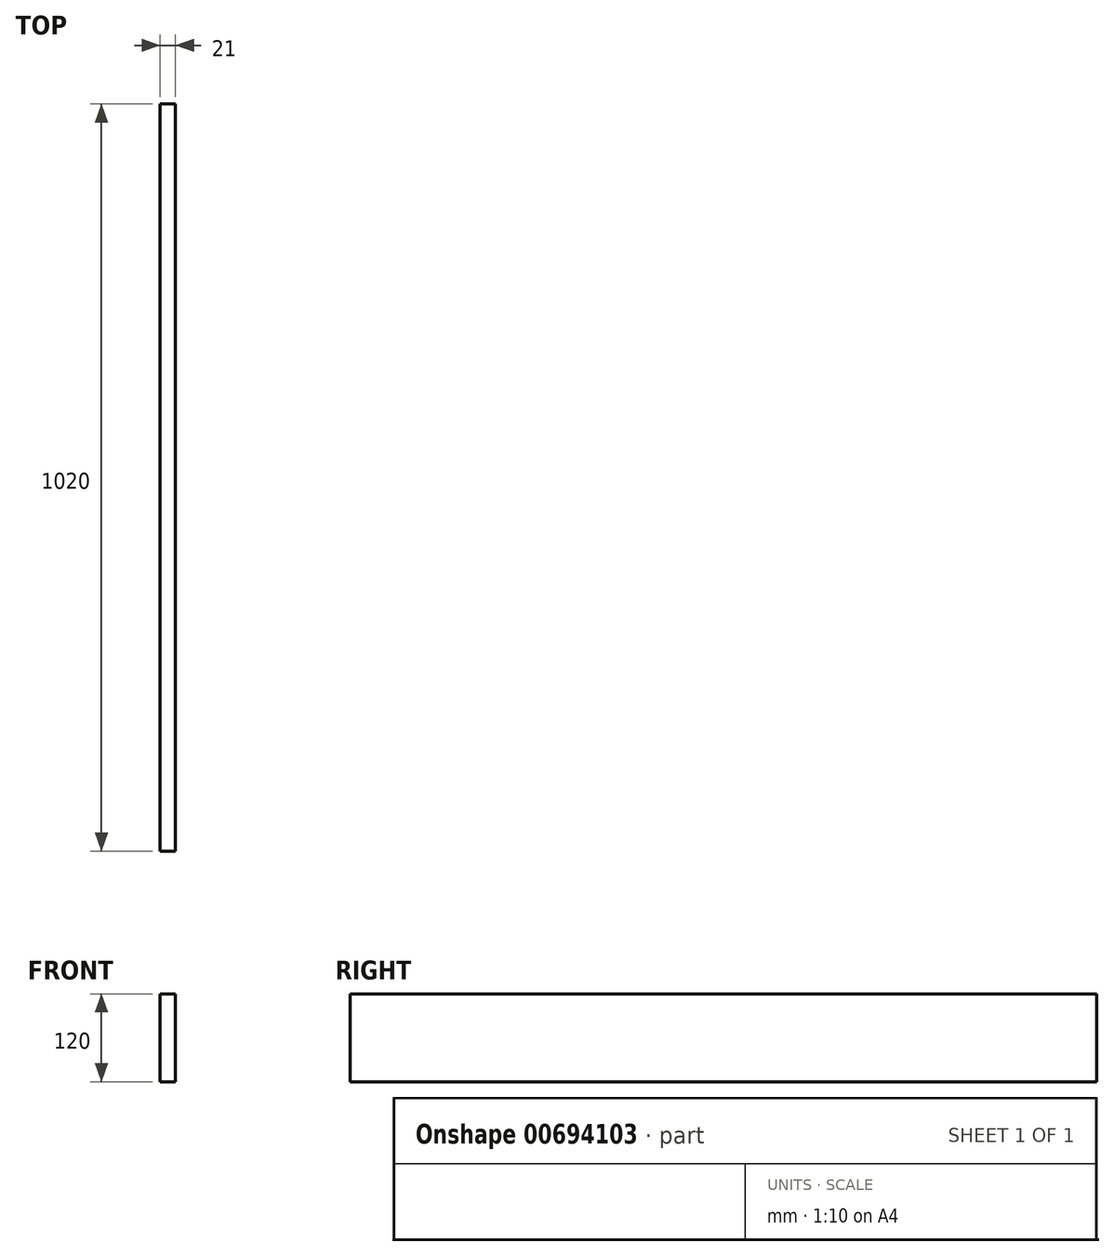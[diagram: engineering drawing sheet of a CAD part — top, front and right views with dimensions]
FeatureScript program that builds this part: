
annotation { "Feature Type Name" : "Feature", "Feature Type Description" : "" }
export const myFeature = defineFeature(function(context is Context, id is Id, definition is map)
    precondition{}
    {
        {
            var Q0;
            Q0=qCreatedBy(makeId("Right.planeOp"),FACE);
            var sketch = newSketch(context, id + "F0", { "sketchPlane" : qUnion([Q0])});
            skLineSegment(sketch, "E0.bottom", {"start": v(-510, -60) * mm, "end": v(510, -60) * mm});
            skLineSegment(sketch, "E0.top", {"start": v(-510, 60) * mm, "end": v(510, 60) * mm});
            skLineSegment(sketch, "E0.left", {"start": v(-510, -60) * mm, "end": v(-510, 60) * mm});
            skLineSegment(sketch, "E0.right", {"start": v(510, -60) * mm, "end": v(510, 60) * mm});
            skSolve(sketch);
        }
        {
            var Q0;
            Q0=makeQuery(id+"F0.imprint","IMPRINT",FACE,{"disambiguationData":[TD([[makeQuery(id+"F0.imprint","IMPRINT",EDGE,{"derivedFrom":sQuery(id+"F0.wireOp",EDGE,"E0.bottom")}),1.0]])]});
            extrude(context, id + "F1", {"entities" : qUnion([Q0]), "depth" : 21 * mm, "offsetDistance" : 25 * mm});
        }
    });
